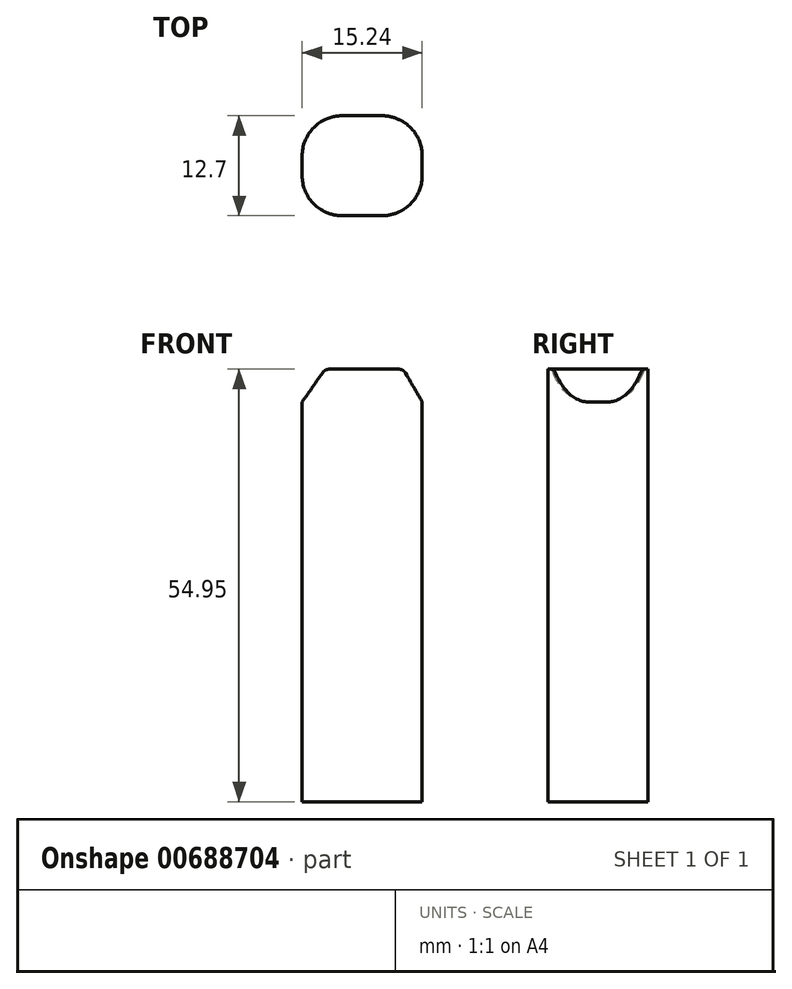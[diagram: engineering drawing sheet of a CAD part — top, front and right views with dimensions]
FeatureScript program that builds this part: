
annotation { "Feature Type Name" : "Feature", "Feature Type Description" : "" }
export const myFeature = defineFeature(function(context is Context, id is Id, definition is map)
    precondition{}
    {
        {
            var Q0;
            Q0=qCreatedBy(makeId("Front.planeOp"),FACE);
            var sketch = newSketch(context, id + "F0", { "sketchPlane" : qUnion([Q0])});
            skLineSegment(sketch, "E0", {"start": v(-11.4, -49.17) * mm, "end": v(3.83, -49.17) * mm});
            skLineSegment(sketch, "E1", {"start": v(3.83, -49.17) * mm, "end": v(3.83, 1.63) * mm});
            skLineSegment(sketch, "E2", {"start": v(-11.4, -49.17) * mm, "end": v(-11.4, 1.63) * mm});
            skLineSegment(sketch, "E3", {"start": v(-11.4, 1.63) * mm, "end": v(-8.48, 5.78) * mm});
            skLineSegment(sketch, "E4", {"start": v(-8.48, 5.78) * mm, "end": v(0, 5.78) * mm});
            skLineSegment(sketch, "E5", {"start": v(0, 5.78) * mm, "end": v(1.43, 5.78) * mm});
            skLineSegment(sketch, "E6", {"start": v(1.43, 5.78) * mm, "end": v(3.83, 1.63) * mm});
            skSolve(sketch);
        }
        {
            var Q0;
            Q0=makeQuery(id+"F0.imprint","IMPRINT",FACE,{"disambiguationData":[TD([[makeQuery(id+"F0.imprint","IMPRINT",EDGE,{"derivedFrom":sQuery(id+"F0.wireOp",EDGE,"E0")}),1.0]])]});
            extrude(context, id + "F1", {"entities" : qUnion([Q0]), "depth" : 12.7 * mm, "offsetDistance" : 25.4 * mm});
        }
        {
            var Q0;
            Q0=makeQuery(id+"F1.opExtrude","CAP_EDGE",EDGE,{"disambiguationData":[OSD([sQuery(id+"F0.wireOp",EDGE,"E2")])],"isStart":true});
            var Q1;
            Q1=makeQuery(id+"F1.opExtrude","CAP_EDGE",EDGE,{"disambiguationData":[OSD([sQuery(id+"F0.wireOp",EDGE,"E2")])],"isStart":false});
            var Q2;
            Q2=makeQuery(id+"F1.opExtrude","CAP_EDGE",EDGE,{"disambiguationData":[OSD([sQuery(id+"F0.wireOp",EDGE,"E1")])],"isStart":false});
            var Q3;
            Q3=makeQuery(id+"F1.opExtrude","CAP_EDGE",EDGE,{"disambiguationData":[OSD([sQuery(id+"F0.wireOp",EDGE,"E1")])],"isStart":true});
            fillet(context, id + "F2", {"entities" : qUnion([Q0, Q1, Q2, Q3]), "radius" : 5.08 * mm, "tangentPropagation" : true, "allowEdgeOverflow" : false});
        }
        {
            var Q0;
            Q0=makeQuery(id+"F1.opExtrude","SWEPT_EDGE",EDGE,{"disambiguationData":[OSD([sQuery(id+"F0.wireOp",EDGE,"E5"),sQuery(id+"F0.wireOp",EDGE,"E6")])]});
            var Q1;
            Q1=makeQuery(id+"F1.opExtrude","SWEPT_EDGE",EDGE,{"disambiguationData":[OSD([sQuery(id+"F0.wireOp",EDGE,"E3"),sQuery(id+"F0.wireOp",EDGE,"E4")])]});
            fillet(context, id + "F3", {"entities" : qUnion([Q0, Q1]), "radius" : 1 * mm, "tangentPropagation" : true, "allowEdgeOverflow" : false});
        }
    });
